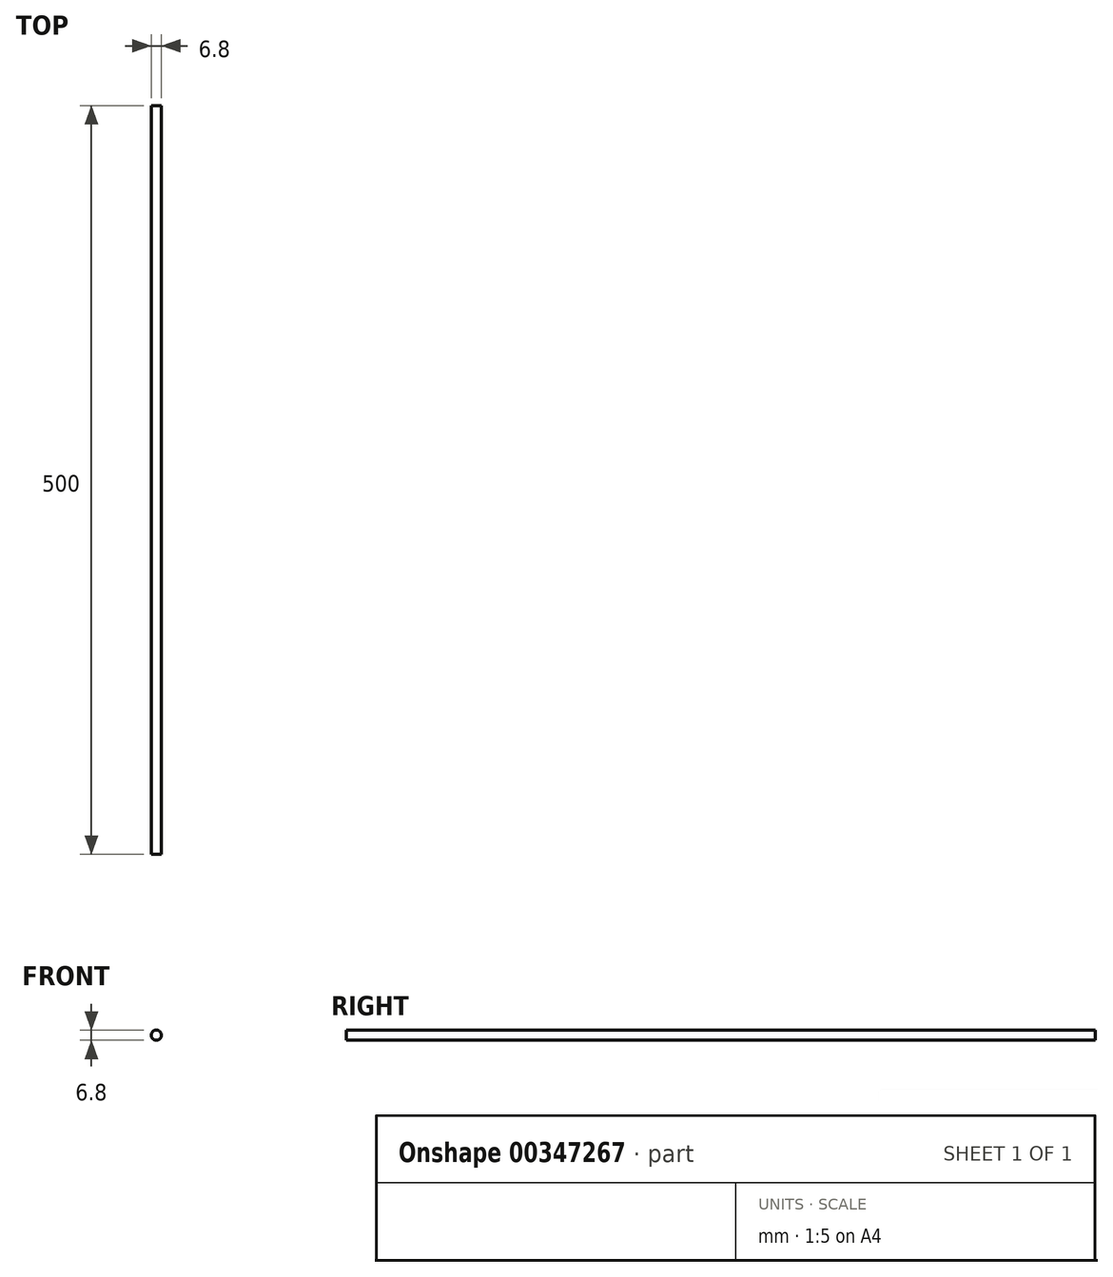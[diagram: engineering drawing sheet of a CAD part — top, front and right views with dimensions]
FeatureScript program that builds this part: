
annotation { "Feature Type Name" : "Feature", "Feature Type Description" : "" }
export const myFeature = defineFeature(function(context is Context, id is Id, definition is map)
    precondition{}
    {
        {
            var Q0;
            Q0=qCreatedBy(makeId("Front.planeOp"),FACE);
            var sketch = newSketch(context, id + "F0", { "sketchPlane" : qUnion([Q0])});
            skCircle(sketch, "E0", {"center": v(0, 0) * mm, "radius": 3.4 * mm});
            skSolve(sketch);
        }
        {
            var Q0;
            Q0 = qSketchRegion(id + "F0", true);
            extrude(context, id + "F1", {"entities" : qUnion([Q0]), "depth" : 500 * mm});
        }
    });
